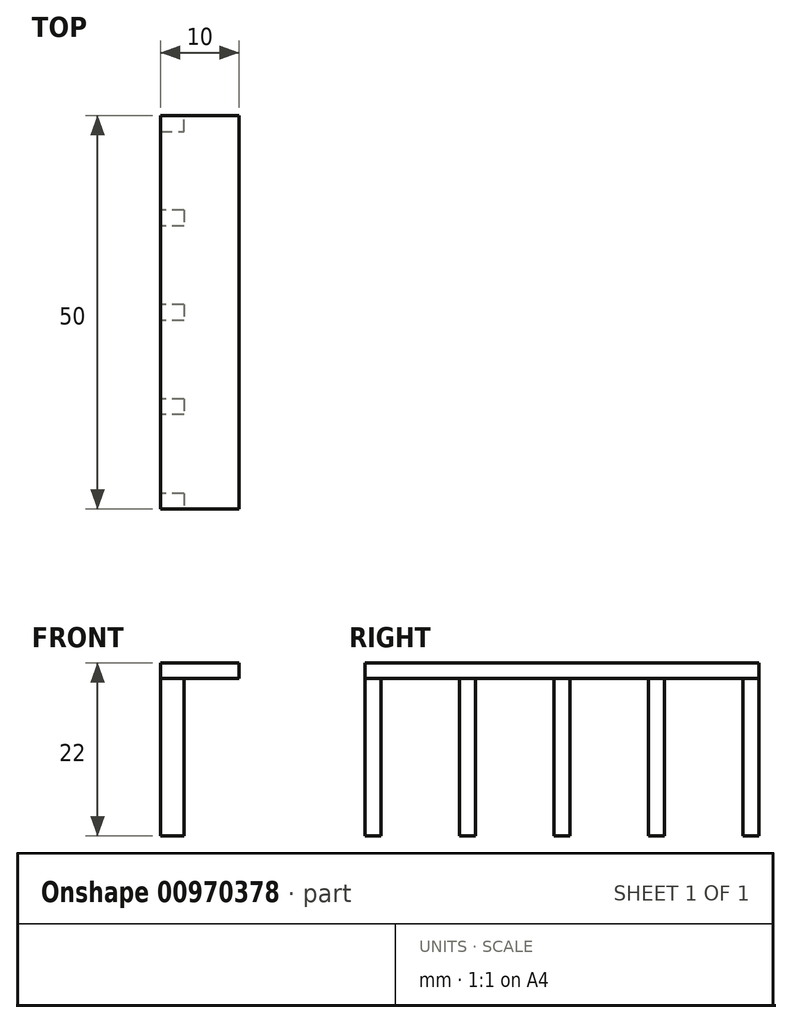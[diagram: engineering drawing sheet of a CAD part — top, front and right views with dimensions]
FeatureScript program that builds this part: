
annotation { "Feature Type Name" : "Feature", "Feature Type Description" : "" }
export const myFeature = defineFeature(function(context is Context, id is Id, definition is map)
    precondition{}
    {
        {
            var Q0;
            Q0=qCreatedBy(makeId("Top.planeOp"),FACE);
            var sketch = newSketch(context, id + "F0", { "sketchPlane" : qUnion([Q0])});
            skLineSegment(sketch, "E0.bottom", {"start": v(0, 0) * mm, "end": v(3, 0) * mm});
            skLineSegment(sketch, "E0.top", {"start": v(0, 2) * mm, "end": v(3, 2) * mm});
            skLineSegment(sketch, "E0.left", {"start": v(0, 0) * mm, "end": v(0, 2) * mm});
            skLineSegment(sketch, "E0.right", {"start": v(3, 0) * mm, "end": v(3, 2) * mm});
            skLineSegment(sketch, "E1", {"start": v(3, 0) * mm, "end": v(3, -10) * mm, "construction": true});
            skLineSegment(sketch, "E2", {"start": v(3, -10) * mm, "end": v(3, -22) * mm, "construction": true});
            skLineSegment(sketch, "E3", {"start": v(3, -22) * mm, "end": v(3, -34) * mm, "construction": true});
            skLineSegment(sketch, "E4", {"start": v(3, -34) * mm, "end": v(3, -46) * mm, "construction": true});
            skLineSegment(sketch, "E5", {"start": v(3, -46) * mm, "end": v(3, -58) * mm, "construction": true});
            skLineSegment(sketch, "E6.bottom", {"start": v(3, -10) * mm, "end": v(0, -10) * mm});
            skLineSegment(sketch, "E6.top", {"start": v(3, -12) * mm, "end": v(0, -12) * mm});
            skLineSegment(sketch, "E6.left", {"start": v(3, -10) * mm, "end": v(3, -12) * mm});
            skLineSegment(sketch, "E6.right", {"start": v(0, -10) * mm, "end": v(0, -12) * mm});
            skLineSegment(sketch, "E7.bottom", {"start": v(3, -22) * mm, "end": v(0, -22) * mm});
            skLineSegment(sketch, "E7.top", {"start": v(3, -24) * mm, "end": v(0, -24) * mm});
            skLineSegment(sketch, "E7.left", {"start": v(3, -22) * mm, "end": v(3, -24) * mm});
            skLineSegment(sketch, "E7.right", {"start": v(0, -22) * mm, "end": v(0, -24) * mm});
            skLineSegment(sketch, "E8.bottom", {"start": v(3, -34) * mm, "end": v(0, -34) * mm});
            skLineSegment(sketch, "E8.top", {"start": v(3, -36) * mm, "end": v(0, -36) * mm});
            skLineSegment(sketch, "E8.left", {"start": v(3, -34) * mm, "end": v(3, -36) * mm});
            skLineSegment(sketch, "E8.right", {"start": v(0, -34) * mm, "end": v(0, -36) * mm});
            skLineSegment(sketch, "E9.bottom", {"start": v(3, -46) * mm, "end": v(0, -46) * mm});
            skLineSegment(sketch, "E9.top", {"start": v(3, -48) * mm, "end": v(0, -48) * mm});
            skLineSegment(sketch, "E9.left", {"start": v(3, -46) * mm, "end": v(3, -48) * mm});
            skLineSegment(sketch, "E9.right", {"start": v(0, -46) * mm, "end": v(0, -48) * mm});
            skLineSegment(sketch, "E10.bottom", {"start": v(3, -58) * mm, "end": v(0, -58) * mm});
            skLineSegment(sketch, "E10.top", {"start": v(3, -60) * mm, "end": v(0, -60) * mm});
            skLineSegment(sketch, "E10.left", {"start": v(3, -58) * mm, "end": v(3, -60) * mm});
            skLineSegment(sketch, "E10.right", {"start": v(0, -58) * mm, "end": v(0, -60) * mm});
            skSolve(sketch);
        }
        {
            var Q0;
            Q0 = qSketchRegion(id + "F0", true);
            extrude(context, id + "F1", {"entities" : qUnion([Q0]), "depth" : 20 * mm, "offsetDistance" : 25 * mm});
        }
        {
            var Q0;
            Q0=makeQuery(id+"F1.opExtrude","CAP_FACE",FACE,{"disambiguationData":[OSD([sQuery(id+"F0.wireOp",EDGE,"E0.bottom"),sQuery(id+"F0.wireOp",EDGE,"E0.top"),sQuery(id+"F0.wireOp",EDGE,"E0.left"),sQuery(id+"F0.wireOp",EDGE,"E0.right")])],"isStart":false});
            var sketch = newSketch(context, id + "F2", { "sketchPlane" : qUnion([Q0])});
            skLineSegment(sketch, "E11.bottom", {"start": v(0, 2) * mm, "end": v(10, 2) * mm});
            skLineSegment(sketch, "E11.top", {"start": v(0, -48) * mm, "end": v(10, -48) * mm});
            skLineSegment(sketch, "E11.left", {"start": v(0, 2) * mm, "end": v(0, -48) * mm});
            skLineSegment(sketch, "E11.right", {"start": v(10, 2) * mm, "end": v(10, -48) * mm});
            skSolve(sketch);
        }
        {
            var Q0;
            {var subQ4=makeQuery(id+"F1.opExtrude","CAP_EDGE",EDGE,{"disambiguationData":[OSD([sQuery(id+"F0.wireOp",EDGE,"E0.bottom")])],"isStart":false});Q0=makeQuery(id+"F2.imprint","IMPRINT",FACE,{"disambiguationData":[TD([[makeQuery(id+"F2.imprint","IMPRINT",EDGE,{"derivedFrom":subQ4}),1.0]])]});}
            var Q1;
            {var subQ3=sQuery(id+"F2.wireOp",EDGE,"E11.top");Q1=makeQuery(id+"F2.imprint","IMPRINT",FACE,{"disambiguationData":[TD([[makeQuery(id+"F2.imprint","IMPRINT",EDGE,{"derivedFrom":subQ3}),1.0]])]});}
            extrude(context, id + "F3", {"entities" : qUnion([Q0, Q1]), "depth" : 2 * mm, "offsetDistance" : 25 * mm});
        }
        {
            var Q0;
            Q0=makeQuery(id+"F1.opExtrude","CAP_FACE",FACE,{"disambiguationData":[OSD([sQuery(id+"F0.wireOp",EDGE,"E10.bottom"),sQuery(id+"F0.wireOp",EDGE,"E10.top"),sQuery(id+"F0.wireOp",EDGE,"E10.left"),sQuery(id+"F0.wireOp",EDGE,"E10.right")])],"isStart":false});
            var sketch = newSketch(context, id + "F4", { "sketchPlane" : qUnion([Q0])});
            skLineSegment(sketch, "E12.bottom", {"start": v(-1.97, -60) * mm, "end": v(5.06, -60) * mm});
            skLineSegment(sketch, "E12.top", {"start": v(-1.97, -56.22) * mm, "end": v(5.06, -56.22) * mm});
            skLineSegment(sketch, "E12.left", {"start": v(-1.97, -60) * mm, "end": v(-1.97, -56.22) * mm});
            skLineSegment(sketch, "E12.right", {"start": v(5.06, -60) * mm, "end": v(5.06, -56.22) * mm});
            skSolve(sketch);
        }
        {
            var Q0;
            Q0 = qSketchRegion(id + "F4", true);
            extrude(context, id + "F5", {"entities" : qUnion([Q0]), "operationType" : NewBodyOperationType.REMOVE, "oppositeDirection" : true, "depth" : 25 * mm, "offsetDistance" : 25 * mm});
        }
    });
